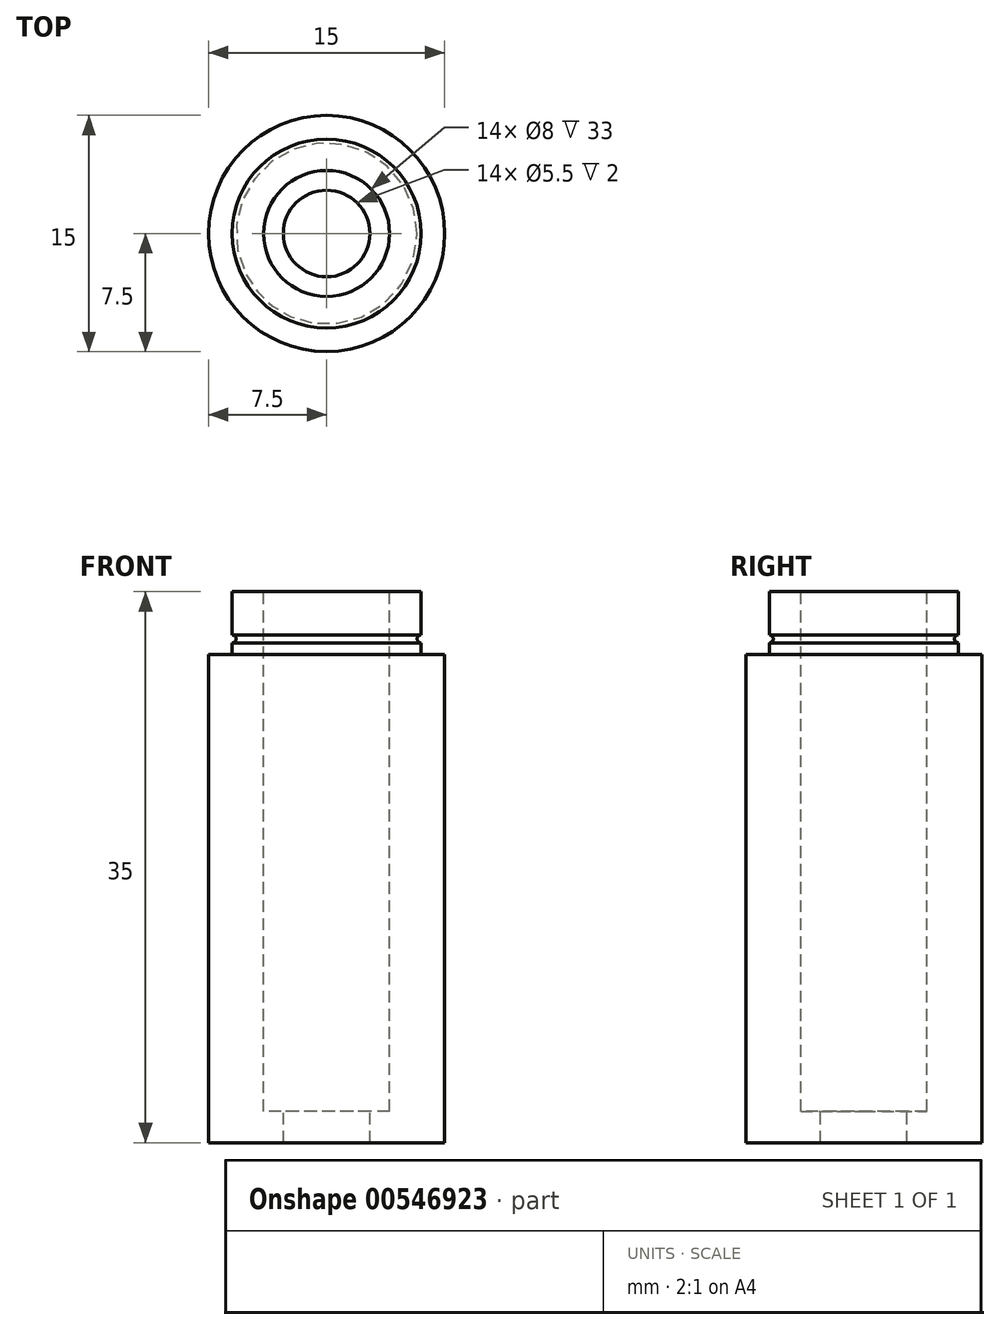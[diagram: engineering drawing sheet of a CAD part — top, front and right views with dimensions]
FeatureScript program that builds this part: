
annotation { "Feature Type Name" : "Feature", "Feature Type Description" : "" }
export const myFeature = defineFeature(function(context is Context, id is Id, definition is map)
    precondition{}
    {
        {
            var Q0;
            Q0=qCreatedBy(makeId("Front.planeOp"),FACE);
            var sketch = newSketch(context, id + "F0", { "sketchPlane" : qUnion([Q0])});
            skLineSegment(sketch, "E0", {"start": v(7.5, -4) * mm, "end": v(7.5, -35) * mm});
            skLineSegment(sketch, "E1", {"start": v(7.5, -4) * mm, "end": v(6, -4) * mm});
            skLineSegment(sketch, "E2", {"start": v(6, -4) * mm, "end": v(6, -3.25) * mm});
            skLineSegment(sketch, "E3", {"start": v(6, 0) * mm, "end": v(4, 0) * mm});
            skLineSegment(sketch, "E4", {"start": v(7.5, -35) * mm, "end": v(2.75, -35) * mm});
            skLineSegment(sketch, "E5", {"start": v(2.75, -35) * mm, "end": v(2.75, -33) * mm});
            skLineSegment(sketch, "E6", {"start": v(2.75, -33) * mm, "end": v(4, -33) * mm});
            skLineSegment(sketch, "E7", {"start": v(4, -33) * mm, "end": v(4, 0) * mm});
            skLineSegment(sketch, "E8", {"start": v(0, 5.95) * mm, "end": v(0, -49.8) * mm, "construction": true});
            skArc(sketch, "E9", {"start": v(6, -2.75) * mm, "mid": v(5.75, -3) * mm, "end": v(6, -3.25) * mm});
            skLineSegment(sketch, "E10.trimOffspring", {"start": v(6, -2.75) * mm, "end": v(6, 0) * mm});
            skSolve(sketch);
        }
        {
            var Q0;
            Q0=makeQuery(id+"F0.imprint","IMPRINT",FACE,{"disambiguationData":[TD([[makeQuery(id+"F0.imprint","IMPRINT",EDGE,{"derivedFrom":sQuery(id+"F0.wireOp",EDGE,"E0")}),-1.0]])]});
            var Q1;
            Q1=sQuery(id+"F0.wireOp",EDGE,"E8");
            var Q2;
            Q2=sQuery(id+"F0.wireOp",EDGE,"E8");
            revolve(context, id + "F1", {"entities" : qUnion([Q0]), "surfaceEntities" : qUnion([Q1]), "axis" : qUnion([Q2]), "revolveType" : RevolveType.FULL});
        }
    });
